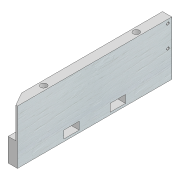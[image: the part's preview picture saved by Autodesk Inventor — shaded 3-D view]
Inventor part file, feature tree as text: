
AUTODESK INVENTOR PART (.ipt)
format: ipt  version: 2022 (Build 260153000, 153)  size: 185,856 bytes
history: native  units: mm
features: sketch x5, extrude x3, hole x3, other x1, chamfer x1
ambient origin geometry x8: Origin, YZ Plane, XZ Plane, XY Plane, X Axis, Y Axis, Z Axis, Center Point
bodies: Body1 (feature_tree)
feature tree (13):
  other  "Твердое тело1"
  extrude  "Выдавливание1"  Depth=200.0mm
  extrude  "Выдавливание2"  Depth=30.0mm
  hole  "Отверстие1"  [1 undecoded]
  hole  "Отверстие2"  [1 undecoded]
  chamfer  "Фаска1"  Distance=12.0mm
  extrude  "Выдавливание3"  Depth=12.0mm TaperAngle=0.0deg
  hole  "Отверстие3"  [1 undecoded]
  sketch  "Эскиз1"
  sketch  "Эскиз2"
  sketch  "Эскиз4"
  sketch  "Эскиз5"
  sketch  "Эскиз6"
note: 3 required parameter values undecoded (feature->parameter linkage not recoverable at this tier; creation-order binding heuristic only, values carry confidence <= 0.55)
